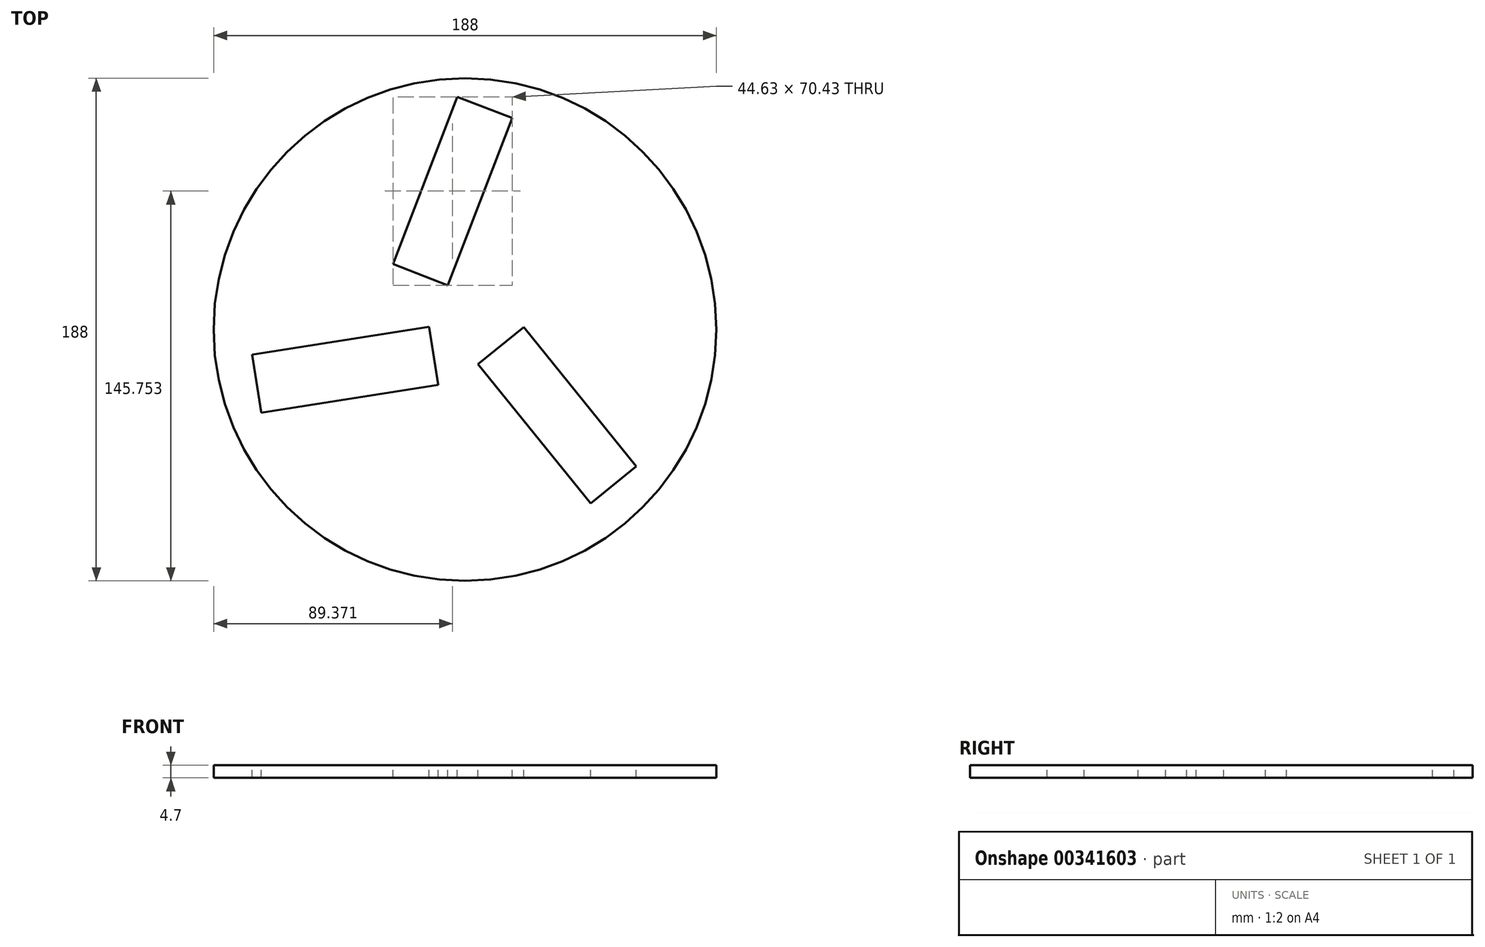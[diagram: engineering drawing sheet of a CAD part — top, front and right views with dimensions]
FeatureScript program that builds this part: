
annotation { "Feature Type Name" : "Feature", "Feature Type Description" : "" }
export const myFeature = defineFeature(function(context is Context, id is Id, definition is map)
    precondition{}
    {
        {
            var Q0;
            Q0=qCreatedBy(makeId("Top.planeOp"),FACE);
            var sketch = newSketch(context, id + "F0", { "sketchPlane" : qUnion([Q0])});
            skCircle(sketch, "E0", {"center": v(0, 3.29) * mm, "radius": 94 * mm});
            skSolve(sketch);
        }
        {
            var Q0;
            Q0=qCreatedBy(makeId("Top.planeOp"),FACE);
            var sketch = newSketch(context, id + "F1", { "sketchPlane" : qUnion([Q0])});
            skLineSegment(sketch, "E1", {"start": v(4.87, -9.65) * mm, "end": v(46.96, -61.78) * mm});
            skLineSegment(sketch, "E2", {"start": v(4.87, -9.65) * mm, "end": v(21.99, 4.17) * mm});
            skLineSegment(sketch, "E3", {"start": v(21.99, 4.17) * mm, "end": v(64.07, -47.96) * mm});
            skLineSegment(sketch, "E4", {"start": v(64.07, -47.96) * mm, "end": v(46.96, -61.78) * mm});
            skSolve(sketch);
        }
        {
            var Q0;
            Q0=makeQuery(id+"F0.imprint","IMPRINT",FACE,{"disambiguationData":[TD([[makeQuery(id+"F0.imprint","IMPRINT",EDGE,{"derivedFrom":sQuery(id+"F0.wireOp",EDGE,"E0")}),1.0]])]});
            extrude(context, id + "F2", {"entities" : qUnion([Q0]), "oppositeDirection" : true, "depth" : 4.7 * mm});
        }
        {
            var Q0;
            Q0=qCreatedBy(makeId("Top.planeOp"),FACE);
            var sketch = newSketch(context, id + "F3", { "sketchPlane" : qUnion([Q0])});
            skLineSegment(sketch, "E5", {"start": v(-6.42, 19.83) * mm, "end": v(17.69, 82.34) * mm});
            skLineSegment(sketch, "E6", {"start": v(17.69, 82.34) * mm, "end": v(-2.84, 90.26) * mm});
            skLineSegment(sketch, "E7", {"start": v(-2.84, 90.26) * mm, "end": v(-26.94, 27.74) * mm});
            skLineSegment(sketch, "E8", {"start": v(-26.94, 27.74) * mm, "end": v(-6.42, 19.83) * mm});
            skSolve(sketch);
        }
        {
            var Q0;
            Q0=qCreatedBy(makeId("Top.planeOp"),FACE);
            var sketch = newSketch(context, id + "F4", { "sketchPlane" : qUnion([Q0])});
            skLineSegment(sketch, "E9", {"start": v(-13.44, 4.25) * mm, "end": v(-79.63, -6.13) * mm});
            skLineSegment(sketch, "E10", {"start": v(-79.63, -6.13) * mm, "end": v(-76.22, -27.86) * mm});
            skLineSegment(sketch, "E11", {"start": v(-76.22, -27.86) * mm, "end": v(-10.03, -17.48) * mm});
            skLineSegment(sketch, "E12", {"start": v(-10.03, -17.48) * mm, "end": v(-13.44, 4.25) * mm});
            skSolve(sketch);
        }
        {
            var Q0;
            Q0 = qSketchRegion(id + "F1", true);
            var Q1;
            Q1 = qSketchRegion(id + "F3", true);
            var Q2;
            Q2 = qSketchRegion(id + "F4", true);
            extrude(context, id + "F5", {"entities" : qUnion([Q0, Q1, Q2]), "operationType" : NewBodyOperationType.REMOVE, "oppositeDirection" : true, "depth" : 4.8 * mm});
        }
    });
